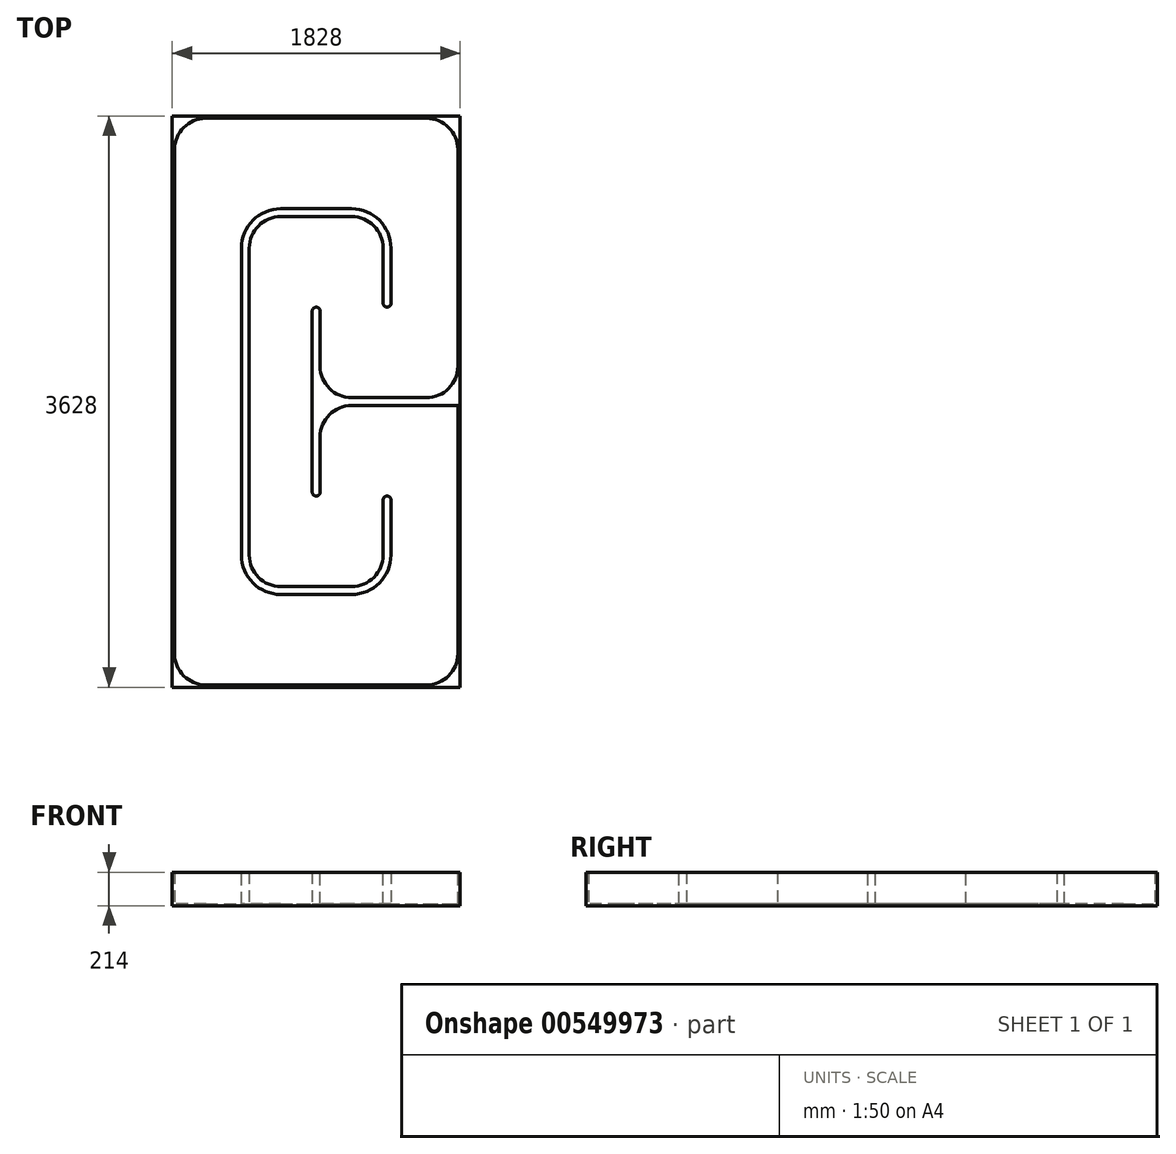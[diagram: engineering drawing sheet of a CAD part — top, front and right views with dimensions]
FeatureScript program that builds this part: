
annotation { "Feature Type Name" : "Feature", "Feature Type Description" : "" }
export const myFeature = defineFeature(function(context is Context, id is Id, definition is map)
    precondition{}
    {
        {
            assignVariable(context, id + "F0", {"name" : "H", "anyValue" : 200});
        }
        {
            assignVariable(context, id + "F1", {"name" : "t", "anyValue" : 14});
        }
        {
            assignVariable(context, id + "F2", {"name" : "w2", "anyValue" : 50});
        }
        {
            assignVariable(context, id + "F3", {"name" : "w3", "anyValue" : getVariable(context, 'w2') / 2});
        }
        {
            assignVariable(context, id + "F4", {"name" : "R1", "anyValue" : 200});
        }
        {
            assignVariable(context, id + "F5", {"name" : "R2", "anyValue" : getVariable(context, 'w3')});
        }
        {
            var Q0;
            Q0=qCreatedBy(makeId("Top.planeOp"),FACE);
            var sketch = newSketch(context, id + "F6", { "sketchPlane" : qUnion([Q0])});
            skLineSegment(sketch, "E0.bottom", {"start": v(-914, 1814) * mm, "end": v(914, 1814) * mm});
            skLineSegment(sketch, "E0.top", {"start": v(-914, -1814) * mm, "end": v(914, -1814) * mm});
            skLineSegment(sketch, "E0.left", {"start": v(-914, 1814) * mm, "end": v(-914, -1814) * mm});
            skLineSegment(sketch, "E0.right", {"start": v(914, 1814) * mm, "end": v(914, -1814) * mm});
            skPoint(sketch, "E0.middle", {"position": v(0, 0) * mm});
            skSolve(sketch);
        }
        {
            var Q0;
            Q0 = qSketchRegion(id + "F6", true);
            extrude(context, id + "F7", {"entities" : qUnion([Q0]), "depth" : (getVariable(context, 'H')) * mm, "offsetDistance" : 25 * mm, "hasSecondDirection" : true, "secondDirectionOppositeDirection" : true, "secondDirectionDepth" : (getVariable(context, 't')) * mm});
        }
        {
            var Q0;
            Q0=makeQuery(id+"F7.opExtrude","CAP_FACE",FACE,{"disambiguationData":[OSD([sQuery(id+"F6.wireOp",EDGE,"E0.bottom"),sQuery(id+"F6.wireOp",EDGE,"E0.top"),sQuery(id+"F6.wireOp",EDGE,"E0.left"),sQuery(id+"F6.wireOp",EDGE,"E0.right")])],"isStart":false});
            shell(context, id + "F8", {"entities" : qUnion([Q0]), "thickness" : (getVariable(context, 't')) * mm});
        }
        {
            var Q0;
            Q0=qCreatedBy(makeId("Top.planeOp"),FACE);
            var sketch = newSketch(context, id + "F9", { "sketchPlane" : qUnion([Q0])});
            skLineSegment(sketch, "E1", {"start": v(-450, 0) * mm, "end": v(-450, 1200) * mm});
            skLineSegment(sketch, "E2", {"start": v(-450, 1200) * mm, "end": v(450, 1200) * mm});
            skLineSegment(sketch, "E3", {"start": v(900, 0) * mm, "end": v(0, 0) * mm});
            skLineSegment(sketch, "E4", {"start": v(0, 0) * mm, "end": v(0, 600) * mm});
            skLineSegment(sketch, "E5.MirrorCS", {"start": v(450, 600) * mm, "end": v(450, 1200) * mm});
            skLineSegment(sketch, "E6.MirrorCS", {"start": v(0, 0) * mm, "end": v(0, -600) * mm});
            skLineSegment(sketch, "E7.MirrorCS", {"start": v(450, -600) * mm, "end": v(450, -1200) * mm});
            skLineSegment(sketch, "E8.MirrorCS", {"start": v(-450, 0) * mm, "end": v(-450, -1200) * mm});
            skLineSegment(sketch, "E9.MirrorCS", {"start": v(-450, -1200) * mm, "end": v(450, -1200) * mm});
            skSolve(sketch);
        }
        {
            var Q0;
            Q0=qCreatedBy(makeId("Front.planeOp"),FACE);
            var Q1;
            Q1=sQuery(id+"F9.wireOp",VERTEX,"E5.MirrorCS.start");
            cPlane(context, id + "F10", {"entities" : qUnion([Q0, Q1]), "cplaneType" : CPlaneType.PLANE_POINT, "offset" : 25 * mm, "width" : 150 * mm, "height" : 150 * mm});
        }
        {
            var Q0;
            Q0=qCreatedBy(id+"F10.planeOp",FACE);
            var sketch = newSketch(context, id + "F11", { "sketchPlane" : qUnion([Q0])});
            skLineSegment(sketch, "E10.bottom", {"start": v(475, 0) * mm, "end": v(425, 0) * mm});
            skLineSegment(sketch, "E10.top", {"start": v(475, 200) * mm, "end": v(425, 200) * mm});
            skLineSegment(sketch, "E10.left", {"start": v(475, 0) * mm, "end": v(475, 200) * mm});
            skLineSegment(sketch, "E10.right", {"start": v(425, 0) * mm, "end": v(425, 200) * mm});
            skLineSegment(sketch, "E11.bottom", {"start": v(25, 0) * mm, "end": v(-25, 0) * mm});
            skLineSegment(sketch, "E11.top", {"start": v(25, 200) * mm, "end": v(-25, 200) * mm});
            skLineSegment(sketch, "E11.left", {"start": v(25, 0) * mm, "end": v(25, 200) * mm});
            skLineSegment(sketch, "E11.right", {"start": v(-25, 0) * mm, "end": v(-25, 200) * mm});
            skPoint(sketch, "E12.0", {"position": v(0, 0) * mm});
            skPoint(sketch, "E13.0", {"position": v(450, 0) * mm});
            skSolve(sketch);
        }
        {
            var Q0;
            Q0=makeQuery(id+"F11.imprint","IMPRINT",FACE,{"disambiguationData":[TD([[makeQuery(id+"F11.imprint","IMPRINT",EDGE,{"derivedFrom":sQuery(id+"F11.wireOp",EDGE,"E10.bottom")}),-1.0]])]});
            var Q1;
            Q1=sQuery(id+"F9.wireOp",EDGE,"E5.MirrorCS");
            var Q2;
            Q2=sQuery(id+"F9.wireOp",EDGE,"E2");
            var Q3;
            Q3=sQuery(id+"F9.wireOp",EDGE,"E1");
            var Q4;
            Q4=sQuery(id+"F9.wireOp",EDGE,"E8.MirrorCS");
            var Q5;
            Q5=sQuery(id+"F9.wireOp",EDGE,"E9.MirrorCS");
            var Q6;
            Q6=sQuery(id+"F9.wireOp",EDGE,"E7.MirrorCS");
            sweep(context, id + "F12", {"profiles" : qUnion([Q0]), "path" : qUnion([Q1, Q2, Q3, Q4, Q5, Q6])});
        }
        {
            var Q0;
            Q0=makeQuery(id+"F11.imprint","IMPRINT",FACE,{"disambiguationData":[TD([[makeQuery(id+"F11.imprint","IMPRINT",EDGE,{"derivedFrom":sQuery(id+"F11.wireOp",EDGE,"E11.bottom")}),-1.0]])]});
            var Q1;
            Q1=sQuery(id+"F9.wireOp",EDGE,"E4");
            var Q2;
            Q2=sQuery(id+"F9.wireOp",EDGE,"E3");
            sweep(context, id + "F13", {"profiles" : qUnion([Q0]), "path" : qUnion([Q1, Q2])});
        }
        {
            var Q0;
            Q0=makeQuery(id+"F11.imprint","IMPRINT",FACE,{"disambiguationData":[TD([[makeQuery(id+"F11.imprint","IMPRINT",EDGE,{"derivedFrom":sQuery(id+"F11.wireOp",EDGE,"E11.bottom")}),-1.0]])]});
            var Q1;
            Q1=sQuery(id+"F9.wireOp",EDGE,"E4");
            var Q2;
            Q2=sQuery(id+"F9.wireOp",EDGE,"E6.MirrorCS");
            sweep(context, id + "F14", {"profiles" : qUnion([Q0]), "path" : qUnion([Q1, Q2])});
        }
        {
            var Q0;
            Q0=makeQuery(id+"F7.opExtrude","SWEPT_BODY",BODY,{"disambiguationData":[OSD([sQuery(id+"F6.wireOp",EDGE,"E0.bottom"),sQuery(id+"F6.wireOp",EDGE,"E0.top"),sQuery(id+"F6.wireOp",EDGE,"E0.left"),sQuery(id+"F6.wireOp",EDGE,"E0.right")])]});
            var Q1;
            Q1=makeQuery(id+"F13.opSweep","SWEPT_BODY",BODY,{"disambiguationData":[OSD([sQuery(id+"F9.wireOp",EDGE,"E3"),sQuery(id+"F11.wireOp",EDGE,"E11.bottom"),sQuery(id+"F11.wireOp",EDGE,"E11.top"),sQuery(id+"F11.wireOp",EDGE,"E11.left"),sQuery(id+"F11.wireOp",EDGE,"E11.right")])]});
            var Q2;
            Q2=makeQuery(id+"F14.opSweep","SWEPT_BODY",BODY,{"disambiguationData":[OSD([sQuery(id+"F9.wireOp",EDGE,"E6.MirrorCS"),sQuery(id+"F11.wireOp",EDGE,"E11.bottom"),sQuery(id+"F11.wireOp",EDGE,"E11.top"),sQuery(id+"F11.wireOp",EDGE,"E11.left"),sQuery(id+"F11.wireOp",EDGE,"E11.right")])]});
            booleanBodies(context, id + "F15", {"operationType" : BooleanOperationType.UNION, "tools" : qUnion([Q0, Q1, Q2])});
        }
        {
            var Q0;
            Q0=makeQuery(id+"F12.opSweep","MID_CAP_EDGE",EDGE,{"disambiguationData":[OSD([sQuery(id+"F9.wireOp",VERTEX,"E1.end"),sQuery(id+"F11.wireOp",EDGE,"E10.right")])],"capPos":2.0});
            var Q1;
            Q1=makeQuery(id+"F12.opSweep","MID_CAP_EDGE",EDGE,{"disambiguationData":[OSD([sQuery(id+"F9.wireOp",VERTEX,"E2.end"),sQuery(id+"F11.wireOp",EDGE,"E10.right")])],"capPos":1.0});
            var Q2;
            Q2=makeQuery(id+"F13.opSweep","MID_CAP_EDGE",EDGE,{"disambiguationData":[OSD([sQuery(id+"F9.wireOp",VERTEX,"E3.end"),sQuery(id+"F11.wireOp",EDGE,"E11.left")])],"capPos":1.0});
            var Q3;
            Q3=makeQuery(id+"F15.opBoolean","INTERSECT",EDGE,{"derivedFrom":[makeQuery(id+"F13.opSweep","SWEPT_FACE",FACE,{"disambiguationData":[OSD([sQuery(id+"F9.wireOp",EDGE,"E3"),sQuery(id+"F11.wireOp",EDGE,"E11.right")])]}),makeQuery(id+"F14.opSweep","SWEPT_FACE",FACE,{"disambiguationData":[OSD([sQuery(id+"F9.wireOp",EDGE,"E4"),sQuery(id+"F11.wireOp",EDGE,"E11.left")])]})]});
            var Q4;
            Q4=makeQuery(id+"F12.opSweep","MID_CAP_EDGE",EDGE,{"disambiguationData":[OSD([sQuery(id+"F9.wireOp",VERTEX,"E9.MirrorCS.start"),sQuery(id+"F11.wireOp",EDGE,"E10.right")])],"capPos":4.0});
            var Q5;
            Q5=makeQuery(id+"F12.opSweep","MID_CAP_EDGE",EDGE,{"disambiguationData":[OSD([sQuery(id+"F9.wireOp",VERTEX,"E7.MirrorCS.end"),sQuery(id+"F11.wireOp",EDGE,"E10.right")])],"capPos":5.0});
            var Q6;
            Q6=makeQuery(id+"F8.opShell","OFFSET_EDGE",EDGE,{"disambiguationData":[OSD([sQuery(id+"F6.wireOp",EDGE,"E0.top"),sQuery(id+"F6.wireOp",EDGE,"E0.right")])]});
            var Q7;
            Q7=makeQuery(id+"F8.opShell","OFFSET_EDGE",EDGE,{"disambiguationData":[OSD([sQuery(id+"F6.wireOp",EDGE,"E0.top"),sQuery(id+"F6.wireOp",EDGE,"E0.left")])]});
            var Q8;
            Q8=makeQuery(id+"F8.opShell","OFFSET_EDGE",EDGE,{"disambiguationData":[OSD([sQuery(id+"F6.wireOp",EDGE,"E0.bottom"),sQuery(id+"F6.wireOp",EDGE,"E0.left")])]});
            var Q9;
            Q9=makeQuery(id+"F8.opShell","OFFSET_EDGE",EDGE,{"disambiguationData":[OSD([sQuery(id+"F6.wireOp",EDGE,"E0.bottom"),sQuery(id+"F6.wireOp",EDGE,"E0.right")])]});
            var Q10;
            Q10=makeQuery(id+"F13.opSweep","CAP_EDGE",EDGE,{"disambiguationData":[OSD([sQuery(id+"F9.wireOp",VERTEX,"E3.start"),sQuery(id+"F11.wireOp",EDGE,"E11.right")])],"isStart":false});
            var Q11;
            Q11=makeQuery(id+"F13.opSweep","CAP_EDGE",EDGE,{"disambiguationData":[OSD([sQuery(id+"F9.wireOp",VERTEX,"E3.start"),sQuery(id+"F11.wireOp",EDGE,"E11.left")])],"isStart":false});
            fillet(context, id + "F16", {"entities" : qUnion([Q0, Q1, Q2, Q3, Q4, Q5, Q6, Q7, Q8, Q9, Q10, Q11]), "radius" : (getVariable(context, 'R1')) * mm, "tangentPropagation" : true, "allowEdgeOverflow" : false});
        }
        {
            var Q0;
            Q0=makeQuery(id+"F12.opSweep","MID_CAP_EDGE",EDGE,{"disambiguationData":[OSD([sQuery(id+"F9.wireOp",VERTEX,"E1.end"),sQuery(id+"F11.wireOp",EDGE,"E10.left")])],"capPos":2.0});
            var Q1;
            Q1=makeQuery(id+"F12.opSweep","MID_CAP_EDGE",EDGE,{"disambiguationData":[OSD([sQuery(id+"F9.wireOp",VERTEX,"E2.end"),sQuery(id+"F11.wireOp",EDGE,"E10.left")])],"capPos":1.0});
            var Q2;
            Q2=makeQuery(id+"F12.opSweep","MID_CAP_EDGE",EDGE,{"disambiguationData":[OSD([sQuery(id+"F9.wireOp",VERTEX,"E9.MirrorCS.start"),sQuery(id+"F11.wireOp",EDGE,"E10.left")])],"capPos":4.0});
            var Q3;
            Q3=makeQuery(id+"F12.opSweep","MID_CAP_EDGE",EDGE,{"disambiguationData":[OSD([sQuery(id+"F9.wireOp",VERTEX,"E7.MirrorCS.end"),sQuery(id+"F11.wireOp",EDGE,"E10.left")])],"capPos":5.0});
            fillet(context, id + "F17", {"entities" : qUnion([Q0, Q1, Q2, Q3]), "radius" : (getVariable(context, 'R1') + getVariable(context, 'w2')) * mm, "tangentPropagation" : true, "allowEdgeOverflow" : false});
        }
        {
            var Q0;
            Q0=makeQuery(id+"F12.opSweep","CAP_EDGE",EDGE,{"disambiguationData":[OSD([sQuery(id+"F9.wireOp",VERTEX,"E5.MirrorCS.start"),sQuery(id+"F11.wireOp",EDGE,"E10.right")])],"isStart":true});
            var Q1;
            Q1=makeQuery(id+"F12.opSweep","CAP_EDGE",EDGE,{"disambiguationData":[OSD([sQuery(id+"F9.wireOp",VERTEX,"E5.MirrorCS.start"),sQuery(id+"F11.wireOp",EDGE,"E10.left")])],"isStart":true});
            var Q2;
            Q2=makeQuery(id+"F13.opSweep","CAP_EDGE",EDGE,{"disambiguationData":[OSD([sQuery(id+"F9.wireOp",VERTEX,"E4.end"),sQuery(id+"F11.wireOp",EDGE,"E11.right")])],"isStart":true});
            var Q3;
            Q3=makeQuery(id+"F13.opSweep","CAP_EDGE",EDGE,{"disambiguationData":[OSD([sQuery(id+"F9.wireOp",VERTEX,"E4.end"),sQuery(id+"F11.wireOp",EDGE,"E11.left")])],"isStart":true});
            var Q4;
            Q4=makeQuery(id+"F14.opSweep","CAP_EDGE",EDGE,{"disambiguationData":[OSD([sQuery(id+"F9.wireOp",VERTEX,"E6.MirrorCS.end"),sQuery(id+"F11.wireOp",EDGE,"E11.right")])],"isStart":false});
            var Q5;
            Q5=makeQuery(id+"F14.opSweep","CAP_EDGE",EDGE,{"disambiguationData":[OSD([sQuery(id+"F9.wireOp",VERTEX,"E6.MirrorCS.end"),sQuery(id+"F11.wireOp",EDGE,"E11.left")])],"isStart":false});
            var Q6;
            Q6=makeQuery(id+"F12.opSweep","CAP_EDGE",EDGE,{"disambiguationData":[OSD([sQuery(id+"F9.wireOp",VERTEX,"E7.MirrorCS.start"),sQuery(id+"F11.wireOp",EDGE,"E10.right")])],"isStart":false});
            var Q7;
            Q7=makeQuery(id+"F12.opSweep","CAP_EDGE",EDGE,{"disambiguationData":[OSD([sQuery(id+"F9.wireOp",VERTEX,"E7.MirrorCS.start"),sQuery(id+"F11.wireOp",EDGE,"E10.left")])],"isStart":false});
            fillet(context, id + "F18", {"entities" : qUnion([Q0, Q1, Q2, Q3, Q4, Q5, Q6, Q7]), "radius" : (getVariable(context, 'R2')) * mm, "tangentPropagation" : true, "allowEdgeOverflow" : false});
        }
    });
